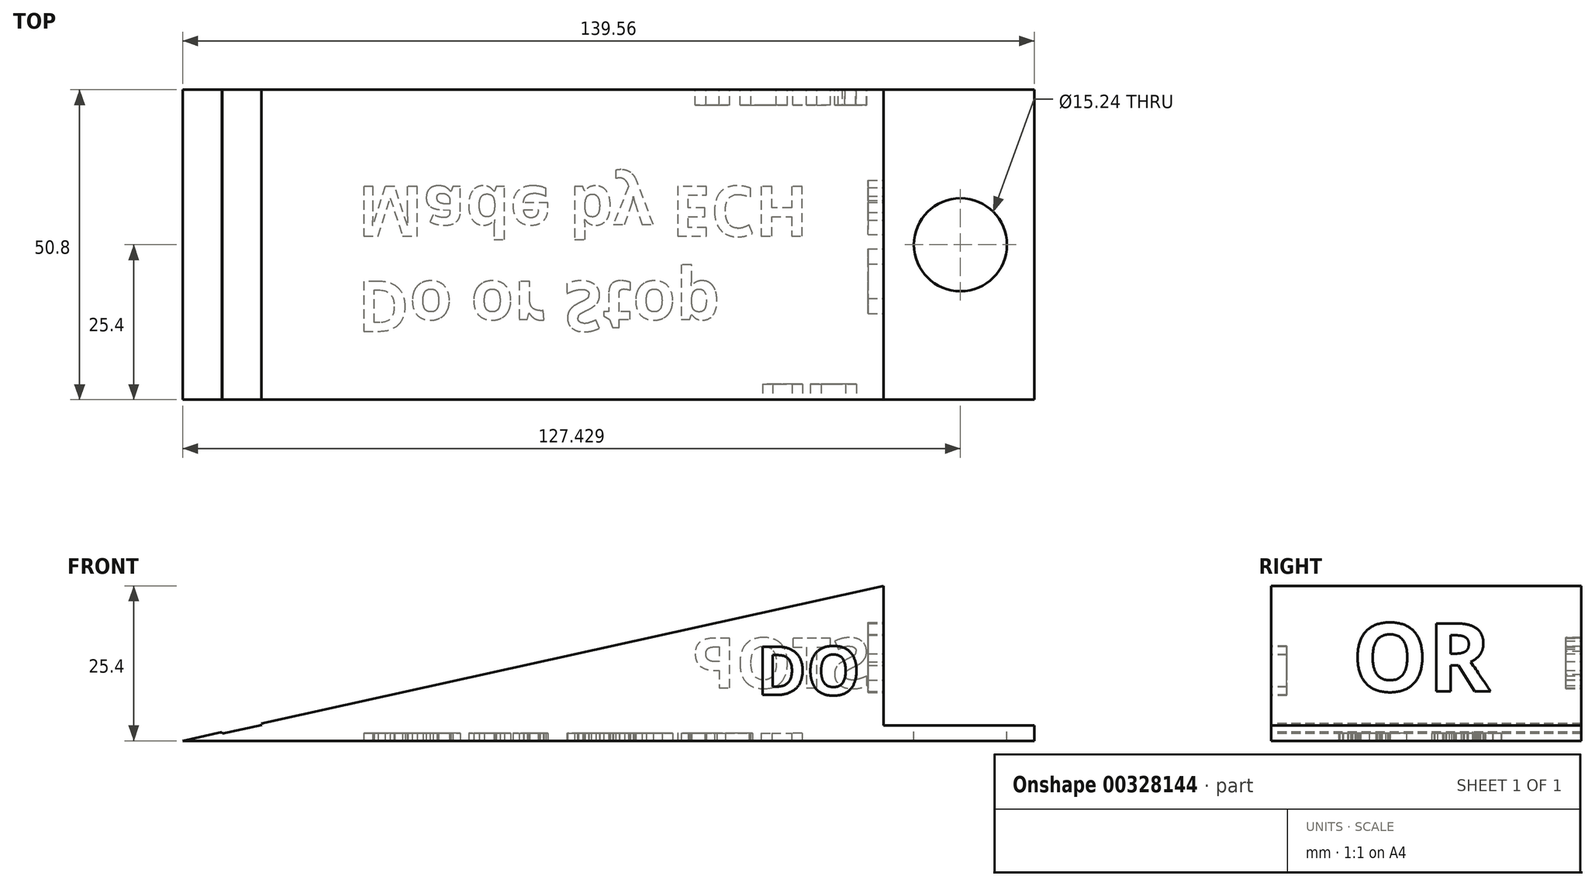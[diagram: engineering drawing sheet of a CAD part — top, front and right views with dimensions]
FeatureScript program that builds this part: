
annotation { "Feature Type Name" : "Feature", "Feature Type Description" : "" }
export const myFeature = defineFeature(function(context is Context, id is Id, definition is map)
    precondition{}
    {
        {
            var Q0;
            Q0=qCreatedBy(makeId("Front.planeOp"),FACE);
            var sketch = newSketch(context, id + "F0", { "sketchPlane" : qUnion([Q0])});
            skLineSegment(sketch, "E0", {"start": v(-63.25, -40.66) * mm, "end": v(51.6, -40.66) * mm});
            skLineSegment(sketch, "E1", {"start": v(51.6, -40.66) * mm, "end": v(51.6, -15.26) * mm});
            skLineSegment(sketch, "E2", {"start": v(51.6, -15.26) * mm, "end": v(-63.25, -40.66) * mm});
            skSolve(sketch);
        }
        {
            var Q0;
            Q0=makeQuery(id+"F0.imprint","IMPRINT",FACE,{"disambiguationData":[TD([[makeQuery(id+"F0.imprint","IMPRINT",EDGE,{"derivedFrom":sQuery(id+"F0.wireOp",EDGE,"E0")}),1.0]])]});
            extrude(context, id + "F1", {"entities" : qUnion([Q0]), "depth" : 25.4 * mm, "hasSecondDirection" : true, "secondDirectionOppositeDirection" : true, "secondDirectionDepth" : 25.4 * mm});
        }
        {
            var Q0;
            Q0=makeQuery(id+"F1.opExtrude","SWEPT_FACE",FACE,{"disambiguationData":[OSD([sQuery(id+"F0.wireOp",EDGE,"E0")])]});
            var sketch = newSketch(context, id + "F2", { "sketchPlane" : qUnion([Q0])});
            skLineSegment(sketch, "E3.bottom", {"start": v(51.6, -25.4) * mm, "end": v(76.3, -25.4) * mm});
            skLineSegment(sketch, "E3.top", {"start": v(51.6, 25.4) * mm, "end": v(76.3, 25.4) * mm});
            skLineSegment(sketch, "E3.left", {"start": v(51.6, -25.4) * mm, "end": v(51.6, 25.4) * mm});
            skLineSegment(sketch, "E3.right", {"start": v(76.3, -25.4) * mm, "end": v(76.3, 25.4) * mm});
            skSolve(sketch);
        }
        {
            var Q0;
            Q0=makeQuery(id+"F2.imprint","IMPRINT",FACE,{"disambiguationData":[TD([[makeQuery(id+"F2.imprint","IMPRINT",EDGE,{"derivedFrom":sQuery(id+"F2.wireOp",EDGE,"E3.bottom")}),1.0]])]});
            extrude(context, id + "F3", {"entities" : qUnion([Q0]), "operationType" : NewBodyOperationType.ADD, "oppositeDirection" : true, "depth" : 2.54 * mm});
        }
        {
            var Q0;
            Q0=makeQuery(id+"F3.opExtrude","CAP_FACE",FACE,{"disambiguationData":[OSD([sQuery(id+"F2.wireOp",EDGE,"E3.bottom"),sQuery(id+"F2.wireOp",EDGE,"E3.top"),sQuery(id+"F2.wireOp",EDGE,"E3.left"),sQuery(id+"F2.wireOp",EDGE,"E3.right")])],"isStart":false});
            var sketch = newSketch(context, id + "F4", { "sketchPlane" : qUnion([Q0])});
            skPoint(sketch, "E4", {"position": v(64.18, 0) * mm});
            skSolve(sketch);
        }
        {
            var Q0;
            Q0=sQuery(id+"F4.wireOp",VERTEX,"E4");
            var Q1;
            Q1=makeQuery(id+"F1.opExtrude","SWEPT_BODY",BODY,{"disambiguationData":[OSD([sQuery(id+"F0.wireOp",EDGE,"E0"),sQuery(id+"F0.wireOp",EDGE,"E1"),sQuery(id+"F0.wireOp",EDGE,"E2")])]});
            hole(context, id + "F5", {"style" : HoleStyle.SIMPLE, "endStyle" : HoleEndStyle.THROUGH, "holeDiameter" : 15.24 * mm, "tappedDepth" : 12.7 * mm, "tapClearance" : 3, "locations" : qUnion([Q0]), "scope" : qUnion([Q1])});
        }
        {
            var Q0;
            Q0=makeQuery(id+"F3.boolean.opBoolean","MERGE",FACE,{"derivedFrom":[makeQuery(id+"F1.opExtrude","SWEPT_FACE",FACE,{"disambiguationData":[OSD([sQuery(id+"F0.wireOp",EDGE,"E0")])]}),makeQuery(id+"F3.opExtrude","CAP_FACE",FACE,{"disambiguationData":[OSD([sQuery(id+"F2.wireOp",EDGE,"E3.bottom"),sQuery(id+"F2.wireOp",EDGE,"E3.top"),sQuery(id+"F2.wireOp",EDGE,"E3.left"),sQuery(id+"F2.wireOp",EDGE,"E3.right")])],"isStart":true})]});
            var sketch = newSketch(context, id + "F6", { "sketchPlane" : qUnion([Q0])});
            skText(sketch, "E5", { "text": "Do or Stop\nMade by ECH", "fontName": "OpenSans-Bold.ttf"});
            const initialGuessF6  = {"E5": [-0.0346, 0.006, 1, 0, 0.00824]};
            skSetInitialGuess(sketch, initialGuessF6);
            skSolve(sketch);
        }
        {
            var Q0;
            Q0 = qSketchRegion(id + "F6", true);
            extrude(context, id + "F7", {"entities" : qUnion([Q0]), "operationType" : NewBodyOperationType.REMOVE, "oppositeDirection" : true, "depth" : 1.27 * mm});
        }
        {
            var Q0;
            Q0=makeQuery(id+"F3.boolean.opBoolean","MERGE",FACE,{"derivedFrom":[makeQuery(id+"F1.opExtrude","CAP_FACE",FACE,{"disambiguationData":[OSD([sQuery(id+"F0.wireOp",EDGE,"E0"),sQuery(id+"F0.wireOp",EDGE,"E1"),sQuery(id+"F0.wireOp",EDGE,"E2")])],"isStart":false}),makeQuery(id+"F3.opExtrude","SWEPT_FACE",FACE,{"disambiguationData":[OSD([sQuery(id+"F2.wireOp",EDGE,"E3.top")])]})]});
            var sketch = newSketch(context, id + "F8", { "sketchPlane" : qUnion([Q0])});
            skText(sketch, "E6", { "text": "DO", "fontName": "OpenSans-Bold.ttf"});
            const initialGuessF8  = {"E6": [0.03075, -0.03315, 1, 0, 0.00798]};
            skSetInitialGuess(sketch, initialGuessF8);
            skSolve(sketch);
        }
        {
            var Q0;
            Q0 = qSketchRegion(id + "F8", true);
            extrude(context, id + "F9", {"entities" : qUnion([Q0]), "operationType" : NewBodyOperationType.REMOVE, "oppositeDirection" : true, "depth" : 2.54 * mm});
        }
        {
            var Q0;
            Q0=makeQuery(id+"F1.opExtrude","SWEPT_FACE",FACE,{"disambiguationData":[OSD([sQuery(id+"F0.wireOp",EDGE,"E1")])]});
            var sketch = newSketch(context, id + "F10", { "sketchPlane" : qUnion([Q0])});
            skText(sketch, "E7", { "text": "OR", "fontName": "OpenSans-Bold.ttf"});
            const initialGuessF10  = {"E7": [-0.01216, -0.03256, 1, 0, 0.01123]};
            skSetInitialGuess(sketch, initialGuessF10);
            skSolve(sketch);
        }
        {
            var Q0;
            Q0 = qSketchRegion(id + "F10", true);
            extrude(context, id + "F11", {"entities" : qUnion([Q0]), "operationType" : NewBodyOperationType.REMOVE, "oppositeDirection" : true, "depth" : 2.54 * mm});
        }
        {
            var Q0;
            Q0=makeQuery(id+"F3.boolean.opBoolean","MERGE",FACE,{"derivedFrom":[makeQuery(id+"F1.opExtrude","CAP_FACE",FACE,{"disambiguationData":[OSD([sQuery(id+"F0.wireOp",EDGE,"E0"),sQuery(id+"F0.wireOp",EDGE,"E1"),sQuery(id+"F0.wireOp",EDGE,"E2")])],"isStart":true}),makeQuery(id+"F3.opExtrude","SWEPT_FACE",FACE,{"disambiguationData":[OSD([sQuery(id+"F2.wireOp",EDGE,"E3.bottom")])]})]});
            var sketch = newSketch(context, id + "F12", { "sketchPlane" : qUnion([Q0])});
            skText(sketch, "E8", { "text": "STOP", "fontName": "OpenSans-Bold.ttf"});
            const initialGuessF12  = {"E8": [-0.0494, -0.03201, 1, 0, 0.00823]};
            skSetInitialGuess(sketch, initialGuessF12);
            skSolve(sketch);
        }
        {
            var Q0;
            Q0 = qSketchRegion(id + "F12", true);
            extrude(context, id + "F13", {"entities" : qUnion([Q0]), "operationType" : NewBodyOperationType.REMOVE, "oppositeDirection" : true, "depth" : 2.54 * mm});
        }
        {
            var Q0;
            Q0=makeQuery(id+"F1.opExtrude","SWEPT_FACE",FACE,{"disambiguationData":[OSD([sQuery(id+"F0.wireOp",EDGE,"E2")])]});
            var sketch = newSketch(context, id + "F14", { "sketchPlane" : qUnion([Q0])});
            skLineSegment(sketch, "E9.bottom", {"start": v(-63.93, 25.4) * mm, "end": v(-57.33, 25.4) * mm});
            skLineSegment(sketch, "E9.top", {"start": v(-63.93, -25.4) * mm, "end": v(-57.33, -25.4) * mm});
            skLineSegment(sketch, "E9.left", {"start": v(-63.93, 25.4) * mm, "end": v(-63.93, -25.4) * mm});
            skLineSegment(sketch, "E9.right", {"start": v(-57.33, 25.4) * mm, "end": v(-57.33, -25.4) * mm});
            skLineSegment(sketch, "E10.1.0.1", {"start": v(-50.73, 25.4) * mm, "end": v(-50.73, -25.4) * mm});
            skLineSegment(sketch, "E10.2.0.0", {"start": v(-50.73, 25.4) * mm, "end": v(-50.73, -25.4) * mm});
            skLineSegment(sketch, "E10.2.0.1", {"start": v(-44.12, 25.4) * mm, "end": v(-44.12, -25.4) * mm});
            skLineSegment(sketch, "E10.3.0.0", {"start": v(-44.12, 25.4) * mm, "end": v(-44.12, -25.4) * mm});
            skLineSegment(sketch, "E10.3.0.1", {"start": v(-37.52, 25.4) * mm, "end": v(-37.52, -25.4) * mm});
            skLineSegment(sketch, "E10.4.0.0", {"start": v(-37.52, 25.4) * mm, "end": v(-37.52, -25.4) * mm});
            skLineSegment(sketch, "E10.4.0.1", {"start": v(-30.91, 25.4) * mm, "end": v(-30.91, -25.4) * mm});
            skLineSegment(sketch, "E10.5.0.0", {"start": v(-30.91, 25.4) * mm, "end": v(-30.91, -25.4) * mm});
            skLineSegment(sketch, "E10.5.0.1", {"start": v(-24.31, 25.4) * mm, "end": v(-24.31, -25.4) * mm});
            skLineSegment(sketch, "E10.6.0.0", {"start": v(-24.31, 25.4) * mm, "end": v(-24.31, -25.4) * mm});
            skLineSegment(sketch, "E10.6.0.1", {"start": v(-17.7, 25.4) * mm, "end": v(-17.7, -25.4) * mm});
            skLineSegment(sketch, "E10.7.0.0", {"start": v(-17.7, 25.4) * mm, "end": v(-17.7, -25.4) * mm});
            skLineSegment(sketch, "E10.7.0.1", {"start": v(-11.1, 25.4) * mm, "end": v(-11.1, -25.4) * mm});
            skLineSegment(sketch, "E10.8.0.0", {"start": v(-11.1, 25.4) * mm, "end": v(-11.1, -25.4) * mm});
            skLineSegment(sketch, "E10.8.0.1", {"start": v(-4.5, 25.4) * mm, "end": v(-4.5, -25.4) * mm});
            skLineSegment(sketch, "E10.9.0.0", {"start": v(-4.5, 25.4) * mm, "end": v(-4.5, -25.4) * mm});
            skLineSegment(sketch, "E10.9.0.1", {"start": v(2.1, 25.4) * mm, "end": v(2.1, -25.4) * mm});
            skLineSegment(sketch, "E10.10.0.0", {"start": v(2.1, 25.4) * mm, "end": v(2.1, -25.4) * mm});
            skLineSegment(sketch, "E10.10.0.1", {"start": v(8.7, 25.4) * mm, "end": v(8.7, -25.4) * mm});
            skLineSegment(sketch, "E10.11.0.0", {"start": v(8.7, 25.4) * mm, "end": v(8.7, -25.4) * mm});
            skLineSegment(sketch, "E10.11.0.1", {"start": v(15.31, 25.4) * mm, "end": v(15.31, -25.4) * mm});
            skLineSegment(sketch, "E10.12.0.0", {"start": v(15.31, 25.4) * mm, "end": v(15.31, -25.4) * mm});
            skLineSegment(sketch, "E10.12.0.1", {"start": v(21.92, 25.4) * mm, "end": v(21.92, -25.4) * mm});
            skLineSegment(sketch, "E10.13.0.0", {"start": v(21.92, 25.4) * mm, "end": v(21.92, -25.4) * mm});
            skLineSegment(sketch, "E10.13.0.1", {"start": v(28.52, 25.4) * mm, "end": v(28.52, -25.4) * mm});
            skLineSegment(sketch, "E10.14.0.0", {"start": v(28.52, 25.4) * mm, "end": v(28.52, -25.4) * mm});
            skLineSegment(sketch, "E10.14.0.1", {"start": v(35.13, 25.4) * mm, "end": v(35.13, -25.4) * mm});
            skLineSegment(sketch, "E10.15.0.0", {"start": v(35.13, 25.4) * mm, "end": v(35.13, -25.4) * mm});
            skLineSegment(sketch, "E10.15.0.1", {"start": v(41.73, 25.4) * mm, "end": v(41.73, -25.4) * mm});
            skLineSegment(sketch, "E10.16.0.0", {"start": v(41.73, 25.4) * mm, "end": v(41.73, -25.4) * mm});
            skLineSegment(sketch, "E10.16.0.1", {"start": v(48.33, 25.4) * mm, "end": v(48.33, -25.4) * mm});
            skLineSegment(sketch, "E10.direction1", {"start": v(-63.93, -25.4) * mm, "end": v(-57.33, -25.4) * mm, "construction": true});
            skSolve(sketch);
        }
        {
            var Q0;
            Q0 = qSketchRegion(id + "F14", true);
            var Q1;
            {var subQ0=sQuery(id+"F14.wireOp",EDGE,"E10.2.0.0");Q1=makeQuery(id+"F14.imprint","IMPRINT",FACE,{"disambiguationData":[TD([[makeQuery(id+"F14.imprint","IMPRINT",EDGE,{"derivedFrom":subQ0}),1.0]])]});}
            var Q2;
            {var subQ0=sQuery(id+"F14.wireOp",EDGE,"E10.8.0.0");Q2=makeQuery(id+"F14.imprint","IMPRINT",FACE,{"disambiguationData":[TD([[makeQuery(id+"F14.imprint","IMPRINT",EDGE,{"derivedFrom":subQ0}),1.0]])]});}
            var Q3;
            {var subQ0=sQuery(id+"F14.wireOp",EDGE,"E10.10.0.0");Q3=makeQuery(id+"F14.imprint","IMPRINT",FACE,{"disambiguationData":[TD([[makeQuery(id+"F14.imprint","IMPRINT",EDGE,{"derivedFrom":subQ0}),1.0]])]});}
            var Q4;
            {var subQ0=sQuery(id+"F14.wireOp",EDGE,"E10.12.0.0");Q4=makeQuery(id+"F14.imprint","IMPRINT",FACE,{"disambiguationData":[TD([[makeQuery(id+"F14.imprint","IMPRINT",EDGE,{"derivedFrom":subQ0}),1.0]])]});}
            var Q5;
            {var subQ0=sQuery(id+"F14.wireOp",EDGE,"E10.14.0.0");Q5=makeQuery(id+"F14.imprint","IMPRINT",FACE,{"disambiguationData":[TD([[makeQuery(id+"F14.imprint","IMPRINT",EDGE,{"derivedFrom":subQ0}),1.0]])]});}
            var Q6;
            {var subQ0=sQuery(id+"F14.wireOp",EDGE,"E10.16.0.0");Q6=makeQuery(id+"F14.imprint","IMPRINT",FACE,{"disambiguationData":[TD([[makeQuery(id+"F14.imprint","IMPRINT",EDGE,{"derivedFrom":subQ0}),1.0]])]});}
            var Q7;
            {var subQ0=sQuery(id+"F14.wireOp",EDGE,"E10.4.0.0");Q7=makeQuery(id+"F14.imprint","IMPRINT",FACE,{"disambiguationData":[TD([[makeQuery(id+"F14.imprint","IMPRINT",EDGE,{"derivedFrom":subQ0}),1.0]])]});}
            var Q8;
            {var subQ0=sQuery(id+"F14.wireOp",EDGE,"E10.6.0.0");Q8=makeQuery(id+"F14.imprint","IMPRINT",FACE,{"disambiguationData":[TD([[makeQuery(id+"F14.imprint","IMPRINT",EDGE,{"derivedFrom":subQ0}),1.0]])]});}
            extrude(context, id + "F15", {"entities" : qUnion([Q0, Q1, Q2, Q3, Q4, Q5, Q6, Q7, Q8]), "operationType" : NewBodyOperationType.REMOVE, "oppositeDirection" : true, "depth" : 0.25 * mm});
        }
    });
